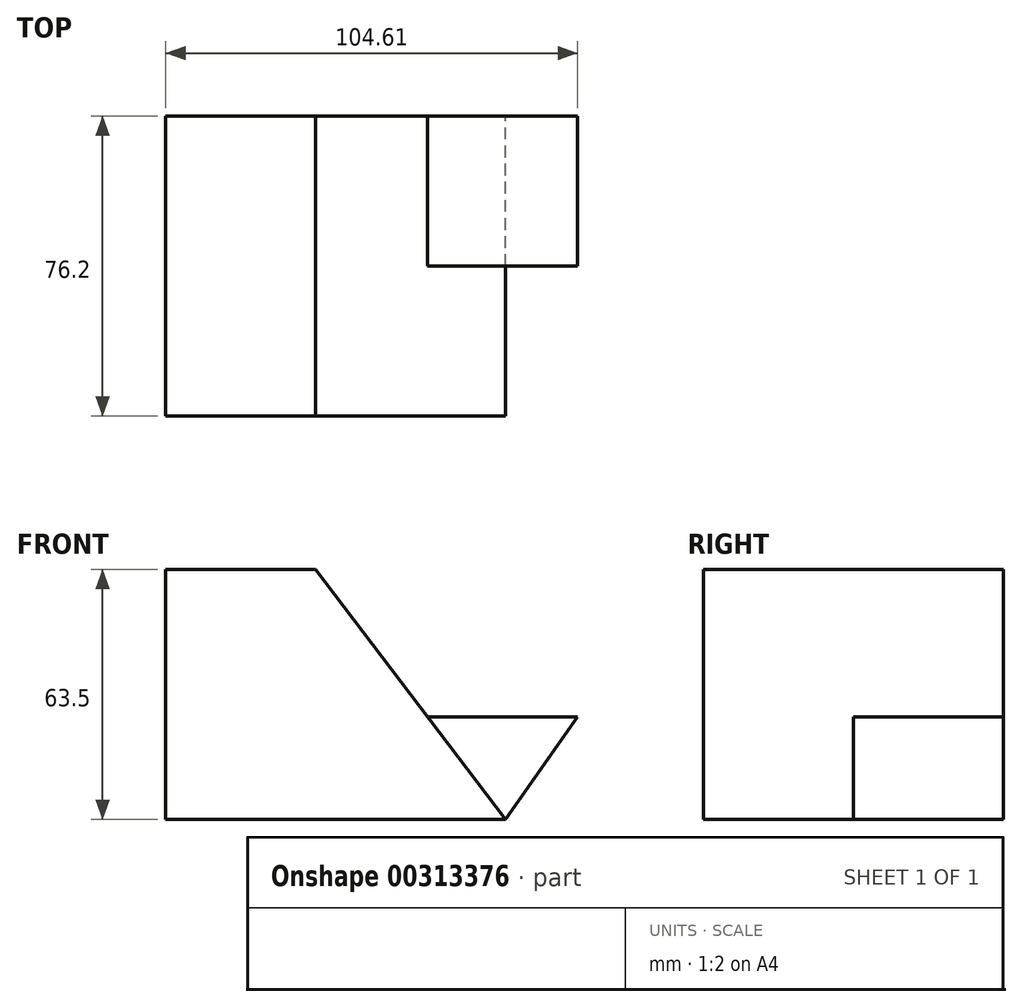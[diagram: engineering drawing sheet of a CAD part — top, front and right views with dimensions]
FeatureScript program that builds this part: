
annotation { "Feature Type Name" : "Feature", "Feature Type Description" : "" }
export const myFeature = defineFeature(function(context is Context, id is Id, definition is map)
    precondition{}
    {
        {
            var Q0;
            Q0=qCreatedBy(makeId("Front.planeOp"),FACE);
            var sketch = newSketch(context, id + "F0", { "sketchPlane" : qUnion([Q0])});
            skLineSegment(sketch, "E0", {"start": v(-41.71, -62.09) * mm, "end": v(47.19, -62.09) * mm});
            skLineSegment(sketch, "E1", {"start": v(-41.71, -62.09) * mm, "end": v(-41.71, 1.41) * mm});
            skLineSegment(sketch, "E2", {"start": v(-41.71, 1.41) * mm, "end": v(-3.61, 1.41) * mm});
            skLineSegment(sketch, "E3", {"start": v(-3.61, 1.41) * mm, "end": v(47.19, -65.5) * mm});
            skSolve(sketch);
        }
        {
            var Q0;
            {var subQ0=sQuery(id+"F0.wireOp",EDGE,"E1");Q0=makeQuery(id+"F0.imprint","IMPRINT",FACE,{"disambiguationData":[TD([[makeQuery(id+"F0.imprint","IMPRINT",EDGE,{"derivedFrom":subQ0}),-1.0]])]});}
            extrude(context, id + "F1", {"entities" : qUnion([Q0]), "depth" : 76.2 * mm});
        }
        {
            var Q0;
            Q0=makeQuery(id+"F1.opExtrude","CAP_FACE",FACE,{"disambiguationData":[OSD([sQuery(id+"F0.wireOp",EDGE,"E0"),sQuery(id+"F0.wireOp",EDGE,"E1"),sQuery(id+"F0.wireOp",EDGE,"E2"),sQuery(id+"F0.wireOp",EDGE,"E3")])],"isStart":true});
            var sketch = newSketch(context, id + "F2", { "sketchPlane" : qUnion([Q0])});
            skLineSegment(sketch, "E4", {"start": v(-24.8, -36.02) * mm, "end": v(-62.9, -36.02) * mm});
            skLineSegment(sketch, "E5", {"start": v(-62.9, -36.02) * mm, "end": v(-44.6, -62.09) * mm});
            skSolve(sketch);
        }
        {
            var Q0;
            Q0 = qSketchRegion(id + "F2", true);
            var Q1;
            {var subQ0=sQuery(id+"F2.wireOp",EDGE,"E4");Q1=makeQuery(id+"F2.imprint","IMPRINT",FACE,{"disambiguationData":[TD([[makeQuery(id+"F2.imprint","IMPRINT",EDGE,{"derivedFrom":subQ0}),1.0]])]});}
            extrude(context, id + "F3", {"entities" : qUnion([Q0, Q1]), "operationType" : NewBodyOperationType.ADD, "oppositeDirection" : true, "depth" : 38.1 * mm});
        }
    });
